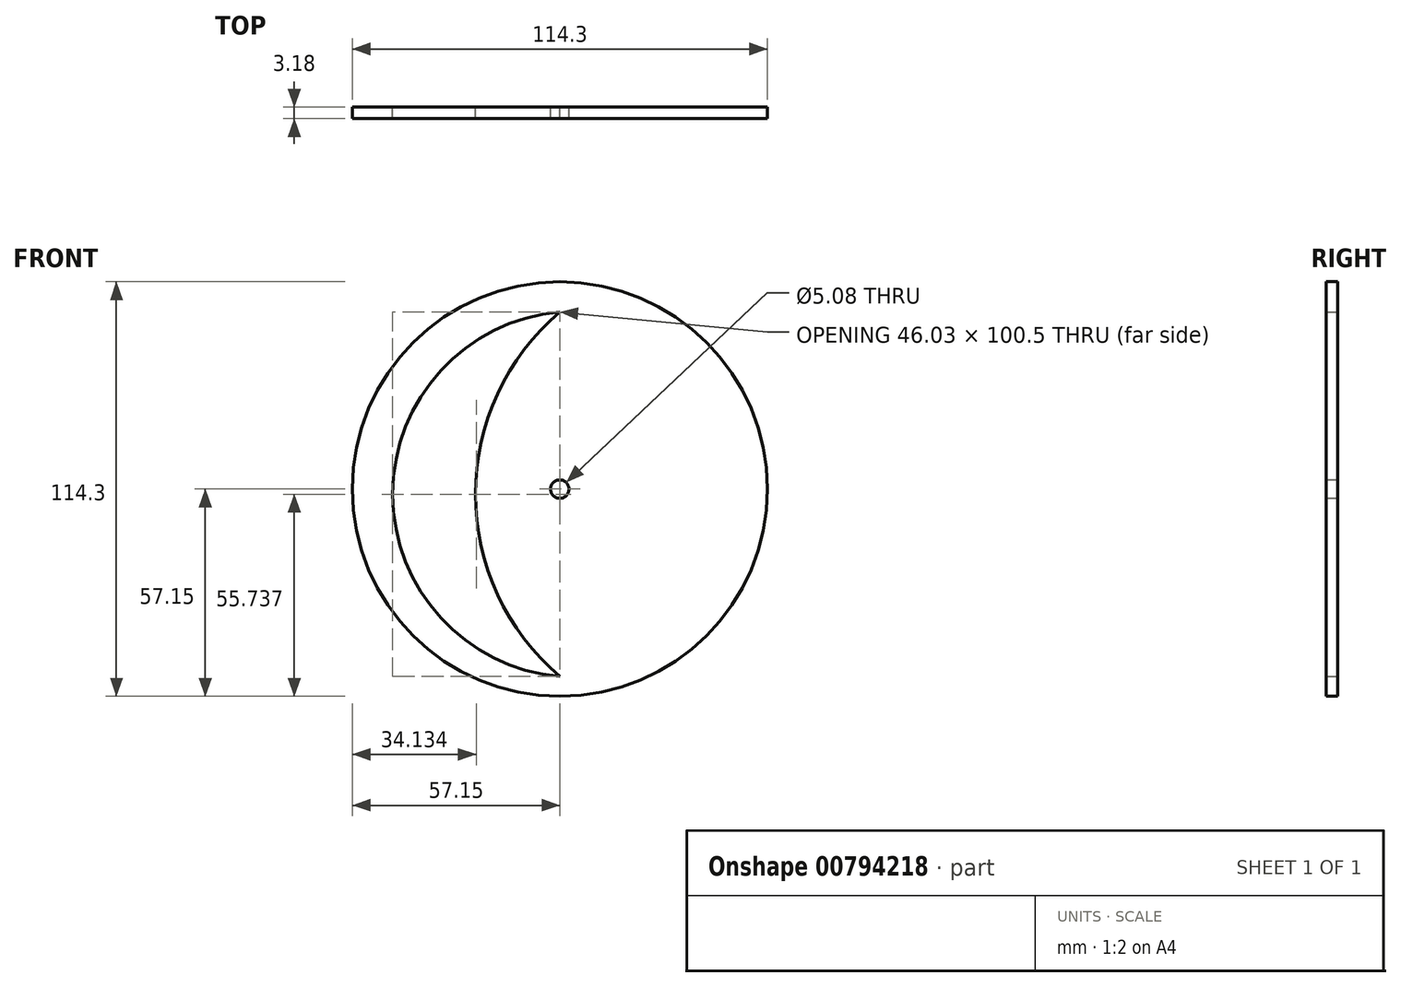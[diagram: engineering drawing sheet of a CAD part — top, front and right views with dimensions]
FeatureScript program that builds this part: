
annotation { "Feature Type Name" : "Feature", "Feature Type Description" : "" }
export const myFeature = defineFeature(function(context is Context, id is Id, definition is map)
    precondition{}
    {
        {
            var Q0;
            Q0=qCreatedBy(makeId("Front.planeOp"),FACE);
            var sketch = newSketch(context, id + "F0", { "sketchPlane" : qUnion([Q0])});
            skCircle(sketch, "E0", {"center": v(0, 0) * mm, "radius": 57.15 * mm});
            skCircle(sketch, "E1", {"center": v(0, 0) * mm, "radius": 2.54 * mm});
            skArc(sketch, "E2", {"start": v(0, 48.84) * mm, "mid": v(-46.03, -1.41) * mm, "end": v(0, -51.66) * mm});
            skArc(sketch, "E3", {"start": v(0, 48.84) * mm, "mid": v(-23.25, -1.41) * mm, "end": v(0, -51.66) * mm});
            skSolve(sketch);
        }
        {
            var Q0;
            Q0=makeQuery(id+"F0.imprint","IMPRINT",FACE,{"disambiguationData":[TD([[makeQuery(id+"F0.imprint","IMPRINT",EDGE,{"derivedFrom":sQuery(id+"F0.wireOp",EDGE,"E0")}),1.0]])]});
            extrude(context, id + "F1", {"entities" : qUnion([Q0]), "depth" : 3.17 * mm, "offsetDistance" : 25.4 * mm});
        }
    });
